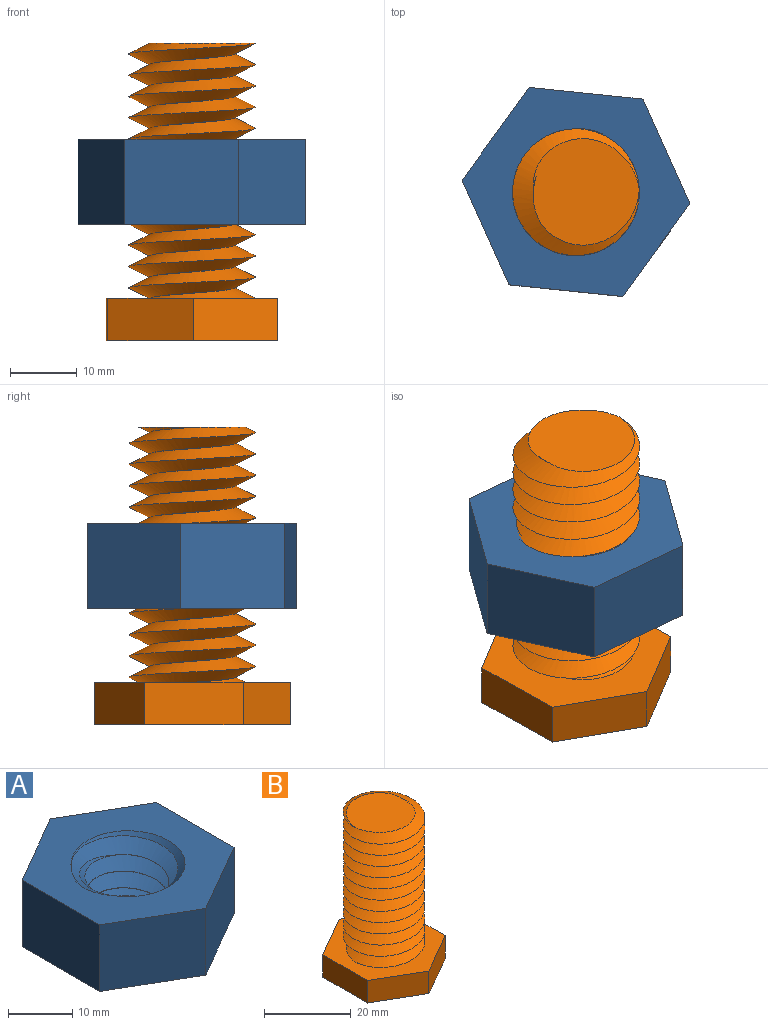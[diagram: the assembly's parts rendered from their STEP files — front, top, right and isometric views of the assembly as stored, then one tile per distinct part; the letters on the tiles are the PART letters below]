
ASSEMBLY  parts=2 mates=1
PART A: 13 faces, bbox 29.7x34.2x16.4 mm
  f0: plane 17.1x12.7mm, normal (1,0,0), area 217.1mm2, adj f1,f5,f7,f8
  f1: plane 14.81x12.7mm, normal (0.5,0.87,0), area 217.1mm2, adj f0,f2,f7,f8
  f2: plane 14.81x12.7mm, normal (-0.5,0.87,0), area 217.1mm2, adj f1,f3,f7,f8
  f3: plane 17.1x12.7mm, normal (-1,0,0), area 217.1mm2, adj f2,f4,f7,f8
  f4: plane 14.81x12.7mm, normal (-0.5,-0.87,0), area 217.1mm2, adj f3,f5,f7,f8
  f5: plane 14.81x12.7mm, normal (0.5,-0.87,0), area 217.1mm2, adj f0,f4,f7,f8
  f6: cylinder r=6.35mm len=12.7mm, axis (0,0,-1), area 2.3mm2, adj f9,f10,f11,f12
  f7: plane 34.24x29.66mm, normal (0,0,1), area 507.4mm2, adj f0,f1,f2,f3,f4,f5,f9,f11
  f8: plane 34.24x29.66mm, normal (0,0,-1), area 507.4mm2, adj f0,f1,f2,f3,f4,f5,f10,f11
  f9: cone r=6.35mm half-angle=45deg, axis (0,0,1), area 73.4mm2, adj f6,f7,f11,f12
  f10: cone r=8.89mm half-angle=45deg, axis (0,0,-1), area 73.4mm2, adj f6,f8,f11,f12
  f11: bspline ~22x19.05mm, area 606mm2, adj f6,f7,f8,f9,f10,f12
  f12: bspline ~22x19.05mm, area 605.7mm2, adj f6,f7,f8,f9,f10,f11
PART B: 12 faces, bbox 27.8x31.8x49 mm
  f0: bspline ~41.26x21.87mm, area 2087mm2, adj f1,f2,f3,f4
  f1: bspline ~41.79x21.87mm, area 2087mm2, adj f0,f2,f3,f4
  f2: cylinder r=6.35mm len=38.1mm, axis (0,0,-1), area 19.1mm2, adj f0,f1,f3,f4
  f3: plane 18.32x18.26mm, normal (0,0,1), area 197.8mm2, adj f0,f1,f2
  f4: plane 31.75x27.82mm, normal (0,0,1), area 361mm2, adj f0,f1,f2,f5,f6,f7,f8,f9
  f5: plane 14.66x6.35mm, normal (1,0,0), area 93.1mm2, adj f4,f6,f10,f11
  f6: plane 12.7x7.33mm, normal (0.5,0.87,0), area 93.1mm2, adj f4,f5,f7,f11
  f7: plane 12.7x7.33mm, normal (-0.5,0.87,0), area 93.1mm2, adj f4,f6,f8,f11
  f8: plane 14.66x6.35mm, normal (-1,0,0), area 93.1mm2, adj f4,f7,f9,f11
  f9: plane 12.7x7.33mm, normal (-0.5,-0.87,0), area 93.1mm2, adj f4,f8,f10,f11
  f10: plane 12.7x7.33mm, normal (0.5,-0.87,0), area 93.1mm2, adj f4,f5,f9,f11
  f11: plane 29.33x25.4mm, normal (0,0,-1), area 558.7mm2, adj f5,f6,f7,f8,f9,f10
PLACE A rot(axis=(0.67,-0.74,0),180deg) t=(-7.16,30.13,96.98)mm fixed
PLACE B rot(axis=(0,0,-1),179deg) t=(-7.17,30.06,66.87)mm
MATE cylindrical A.f8 <-> B.f2  axis (0,0,1) through (-7.17,30.06,96.98)mm
